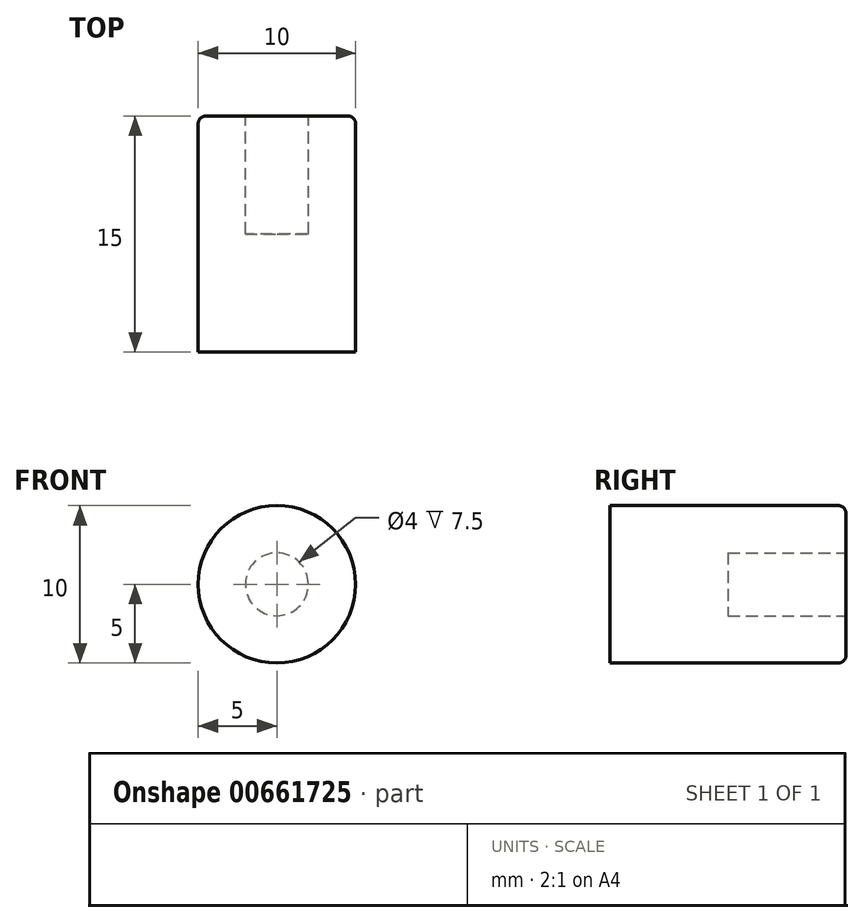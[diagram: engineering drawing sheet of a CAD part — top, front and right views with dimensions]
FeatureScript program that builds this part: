
annotation { "Feature Type Name" : "Feature", "Feature Type Description" : "" }
export const myFeature = defineFeature(function(context is Context, id is Id, definition is map)
    precondition{}
    {
        {
            var Q0;
            Q0=qCreatedBy(makeId("Front.planeOp"),FACE);
            var sketch = newSketch(context, id + "F0", { "sketchPlane" : qUnion([Q0])});
            skCircle(sketch, "E0", {"center": v(0, 0) * mm, "radius": 5 * mm});
            skSolve(sketch);
        }
        {
            var Q0;
            Q0=makeQuery(id+"F0.imprint","IMPRINT",FACE,{"disambiguationData":[TD([[makeQuery(id+"F0.imprint","IMPRINT",EDGE,{"derivedFrom":sQuery(id+"F0.wireOp",EDGE,"E0")}),1.0]])]});
            extrude(context, id + "F1", {"entities" : qUnion([Q0]), "depth" : 15 * mm, "offsetDistance" : 25 * mm});
        }
        {
            var Q0;
            Q0=makeQuery(id+"F1.opExtrude","CAP_EDGE",EDGE,{"disambiguationData":[OSD([sQuery(id+"F0.wireOp",EDGE,"E0")])],"isStart":true});
            fillet(context, id + "F2", {"entities" : qUnion([Q0]), "radius" : 0.5 * mm, "tangentPropagation" : true, "allowEdgeOverflow" : false});
        }
        {
            var Q0;
            Q0=makeQuery(id+"F1.opExtrude","CAP_FACE",FACE,{"disambiguationData":[OSD([sQuery(id+"F0.wireOp",EDGE,"E0")])],"isStart":true});
            var sketch = newSketch(context, id + "F3", { "sketchPlane" : qUnion([Q0])});
            skCircle(sketch, "E1", {"center": v(0, 0) * mm, "radius": 2 * mm});
            skSolve(sketch);
        }
        {
            var Q0;
            Q0=makeQuery(id+"F3.imprint","IMPRINT",FACE,{"disambiguationData":[TD([[makeQuery(id+"F3.imprint","IMPRINT",EDGE,{"derivedFrom":sQuery(id+"F3.wireOp",EDGE,"E1")}),1.0]])]});
            extrude(context, id + "F4", {"entities" : qUnion([Q0]), "operationType" : NewBodyOperationType.REMOVE, "oppositeDirection" : true, "depth" : 7.5 * mm, "offsetDistance" : 25 * mm});
        }
    });
